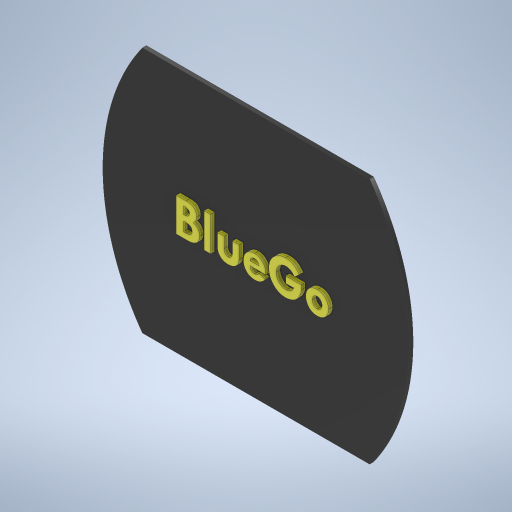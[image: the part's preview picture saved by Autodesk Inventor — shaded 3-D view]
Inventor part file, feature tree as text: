
AUTODESK INVENTOR PART (.ipt)
format: ipt  version: 2024.3 (Build 283343000, 343)  size: 343,040 bytes
history: native  units: mm
features: sketch x3, extrude x2
ambient origin geometry x8: Origin, YZ Plane, XZ Plane, XY Plane, X Axis, Y Axis, Z Axis, Center Point
bodies: Solid1 (feature_tree)
feature tree (5):
  extrude  "Extrusion1"  Depth=125.0mm
  extrude  "Extrusion2"  Depth=20.0mm
  sketch  "Sketch3"  dims[d4=2.0mm d5=0.0mm d6=2.0mm d7=0.0mm]
  sketch  "Sketch1"  dims[d0=115.0mm d1=125.0mm]
  sketch  "Sketch2"  dims[d2=20.0mm d3=20.0mm]
